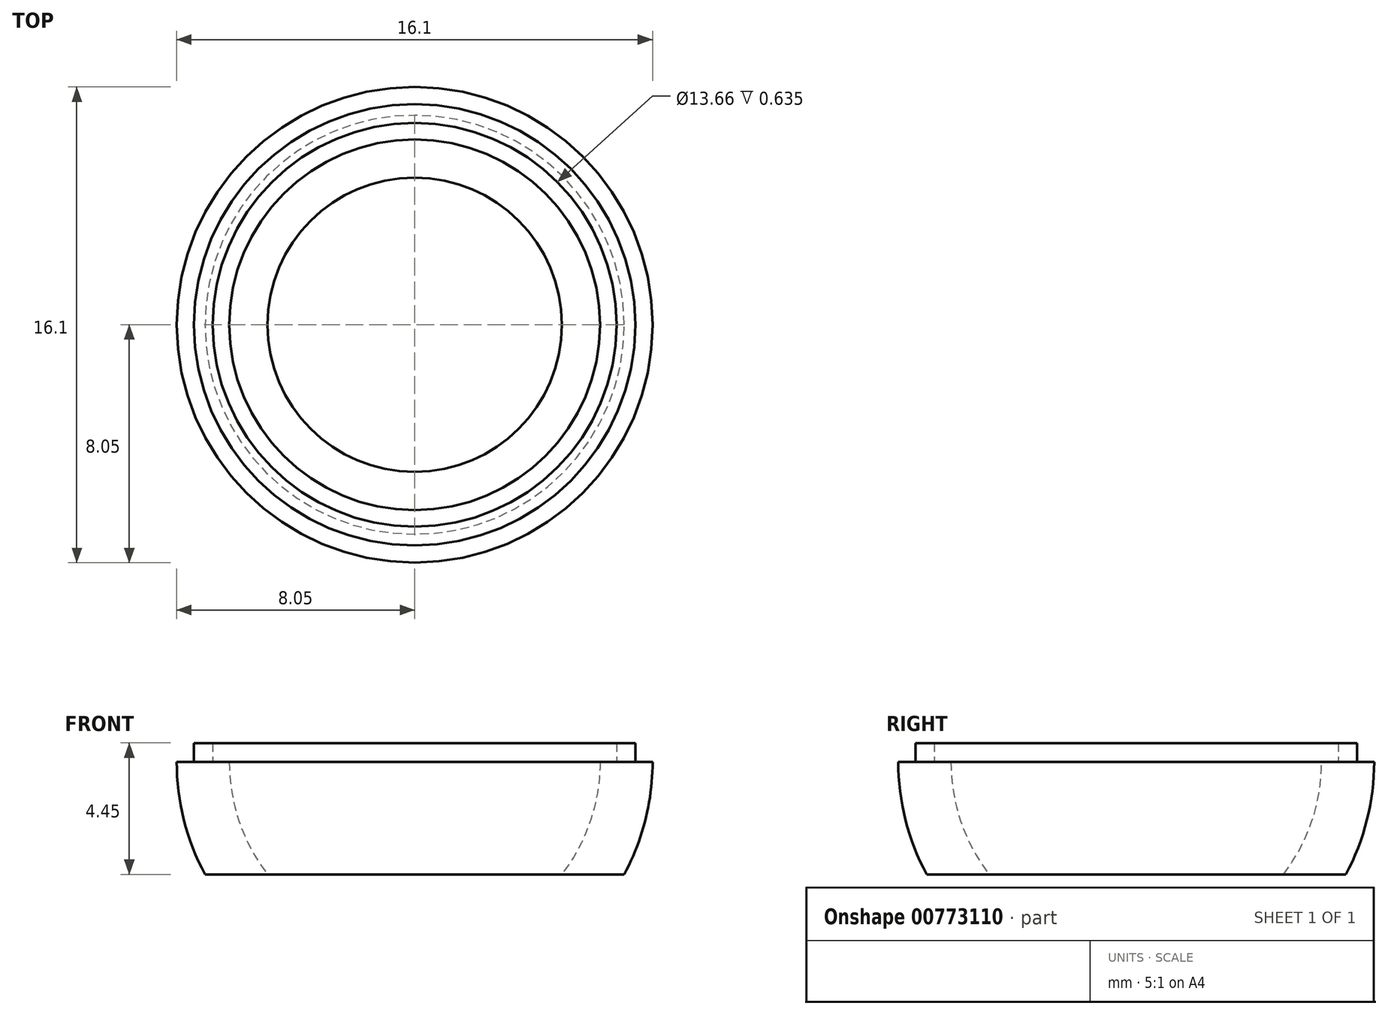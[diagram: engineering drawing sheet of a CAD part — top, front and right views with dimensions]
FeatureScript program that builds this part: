
annotation { "Feature Type Name" : "Feature", "Feature Type Description" : "" }
export const myFeature = defineFeature(function(context is Context, id is Id, definition is map)
    precondition{}
    {
        {
            var Q0;
            Q0=qCreatedBy(makeId("Front.planeOp"),FACE);
            var sketch = newSketch(context, id + "F0", { "sketchPlane" : qUnion([Q0])});
            skCircle(sketch, "E0", {"center": v(0, 0) * mm, "radius": 5 * mm, "construction": true});
            skLineSegment(sketch, "E1", {"start": v(0, 8.05) * mm, "end": v(0, -8.05) * mm});
            skArc(sketch, "E2", {"start": v(0, -8.05) * mm, "mid": v(8.05, 0) * mm, "end": v(0, 8.05) * mm});
            skSolve(sketch);
        }
        {
            var Q0;
            Q0=makeQuery(id+"F0.imprint","IMPRINT",FACE,{"disambiguationData":[TD([[makeQuery(id+"F0.imprint","IMPRINT",EDGE,{"derivedFrom":sQuery(id+"F0.wireOp",EDGE,"E1")}),1.0]])]});
            var Q1;
            Q1=sQuery(id+"F0.wireOp",EDGE,"E1");
            revolve(context, id + "F1", {"surfaceOperationType" : NewSurfaceOperationType.NEW, "entities" : qUnion([Q0]), "axis" : qUnion([Q1]), "revolveType" : RevolveType.FULL});
        }
        {
            var Q0;
            Q0=qCreatedBy(makeId("Front.planeOp"),FACE);
            var sketch = newSketch(context, id + "F2", { "sketchPlane" : qUnion([Q0])});
            skLineSegment(sketch, "E3", {"start": v(0, 6.27) * mm, "end": v(0, -6.27) * mm});
            skArc(sketch, "E4", {"start": v(0, -6.27) * mm, "mid": v(6.27, 0) * mm, "end": v(0, 6.27) * mm});
            skSolve(sketch);
        }
        {
            var Q0;
            Q0=qSketchRegion(id+"F2",true);
            var Q1;
            Q1=sQuery(id+"F2.wireOp",EDGE,"E3");
            revolve(context, id + "F3", {"operationType" : NewBodyOperationType.REMOVE, "surfaceOperationType" : NewSurfaceOperationType.NEW, "entities" : qUnion([Q0]), "axis" : qUnion([Q1]), "revolveType" : RevolveType.FULL, "oppositeDirection" : true});
        }
        {
            var Q0;
            Q0=qCreatedBy(makeId("Top.planeOp"),FACE);
            var sketch = newSketch(context, id + "F4", { "sketchPlane" : qUnion([Q0])});
            skCircle(sketch, "E5", {"center": v(0, 0) * mm, "radius": 12.7 * mm});
            skSolve(sketch);
        }
        {
            var Q0;
            Q0 = qSketchRegion(id + "F4", true);
            extrude(context, id + "F5", {"entities" : qUnion([Q0]), "operationType" : NewBodyOperationType.REMOVE, "depth" : 25.4 * mm, "offsetDistance" : 25.4 * mm});
        }
        {
            var Q0;
            Q0=qCreatedBy(makeId("Top.planeOp"),FACE);
            cPlane(context, id + "F6", {"entities" : qUnion([Q0]), "cplaneType" : CPlaneType.OFFSET, "offset" : 3.8 * mm, "oppositeDirection" : true, "width" : 152.4 * mm, "height" : 152.4 * mm});
        }
        {
            var Q0;
            Q0=qCreatedBy(id+"F6.planeOp",FACE);
            var sketch = newSketch(context, id + "F7", { "sketchPlane" : qUnion([Q0])});
            skCircle(sketch, "E6", {"center": v(0, 0) * mm, "radius": 12.7 * mm});
            skSolve(sketch);
        }
        {
            var Q0;
            Q0 = qSketchRegion(id + "F7", true);
            extrude(context, id + "F8", {"entities" : qUnion([Q0]), "operationType" : NewBodyOperationType.REMOVE, "oppositeDirection" : true, "depth" : 25.4 * mm, "offsetDistance" : 25.4 * mm});
        }
        {
            var Q0;
            Q0=makeQuery(id+"F5.boolean.opBoolean","COPY",FACE,{"derivedFrom":makeQuery(id+"F5.opExtrude","CAP_FACE",FACE,{"disambiguationData":[OSD([sQuery(id+"F4.wireOp",EDGE,"E5")])],"isStart":true})});
            var sketch = newSketch(context, id + "F9", { "sketchPlane" : qUnion([Q0])});
            skCircle(sketch, "E7", {"center": v(0, 0) * mm, "radius": 6.83 * mm});
            skCircle(sketch, "E8", {"center": v(0, 0) * mm, "radius": 7.46 * mm});
            skSolve(sketch);
        }
        {
            var Q0;
            Q0 = qSketchRegion(id + "F9", true);
            extrude(context, id + "F10", {"entities" : qUnion([Q0]), "operationType" : NewBodyOperationType.ADD, "depth" : 0.64 * mm, "offsetDistance" : 25.4 * mm});
        }
    });
